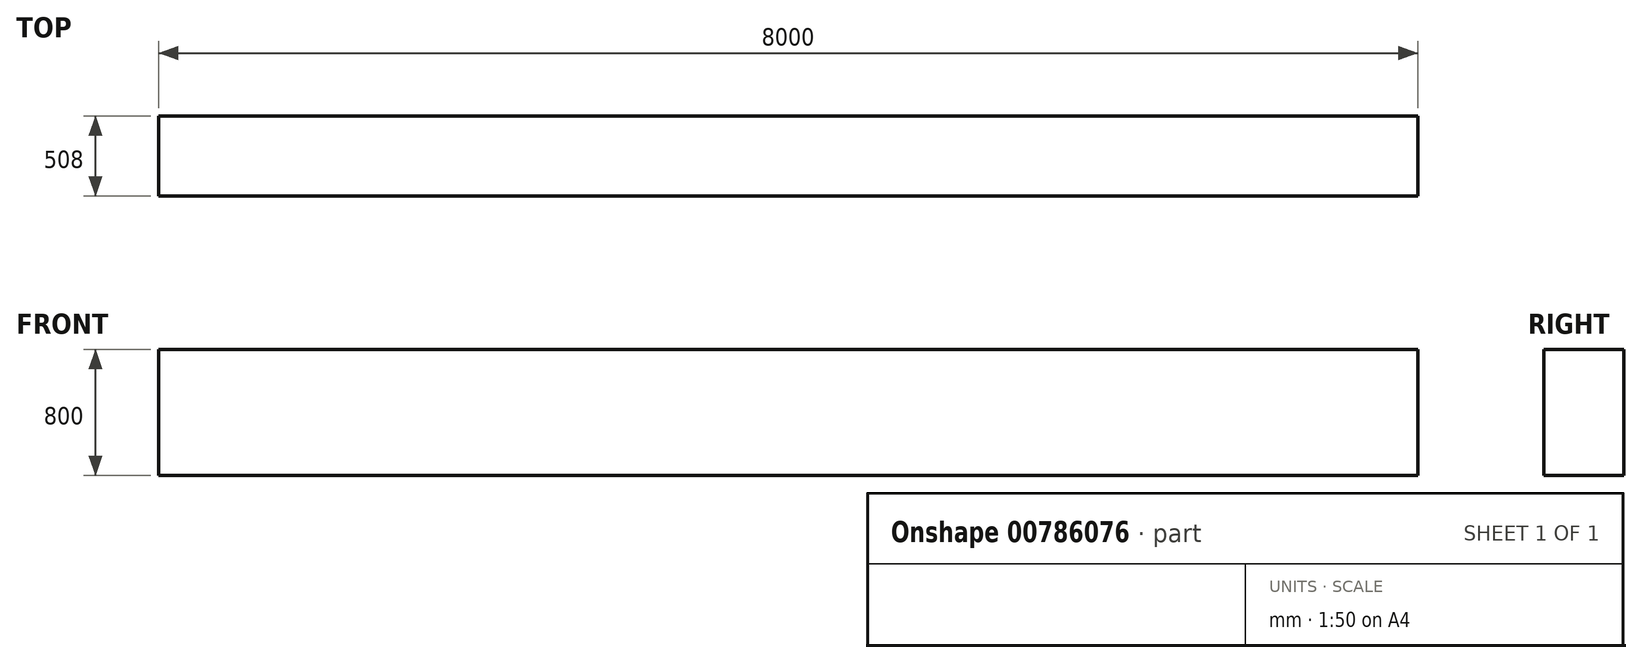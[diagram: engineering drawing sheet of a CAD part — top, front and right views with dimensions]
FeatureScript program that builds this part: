
annotation { "Feature Type Name" : "Feature", "Feature Type Description" : "" }
export const myFeature = defineFeature(function(context is Context, id is Id, definition is map)
    precondition{}
    {
        {
            var Q0;
            Q0=qCreatedBy(makeId("Front.planeOp"),FACE);
            var sketch = newSketch(context, id + "F0", { "sketchPlane" : qUnion([Q0])});
            skLineSegment(sketch, "E0.bottom", {"start": v(-4009.6, 403.08) * mm, "end": v(3990.4, 403.08) * mm});
            skLineSegment(sketch, "E0.top", {"start": v(-4009.6, -396.92) * mm, "end": v(3990.4, -396.92) * mm});
            skLineSegment(sketch, "E0.left", {"start": v(-4009.6, 403.08) * mm, "end": v(-4009.6, -396.92) * mm});
            skLineSegment(sketch, "E0.right", {"start": v(3990.4, 403.08) * mm, "end": v(3990.4, -396.92) * mm});
            skSolve(sketch);
        }
        {
            var Q0;
            Q0=makeQuery(id+"F0.imprint","IMPRINT",FACE,{"disambiguationData":[TD([[makeQuery(id+"F0.imprint","IMPRINT",EDGE,{"derivedFrom":sQuery(id+"F0.wireOp",EDGE,"E0.bottom")}),-1.0]])]});
            extrude(context, id + "F1", {"entities" : qUnion([Q0]), "oppositeDirection" : true, "depth" : 508 * mm, "offsetDistance" : 25.4 * mm});
        }
    });
